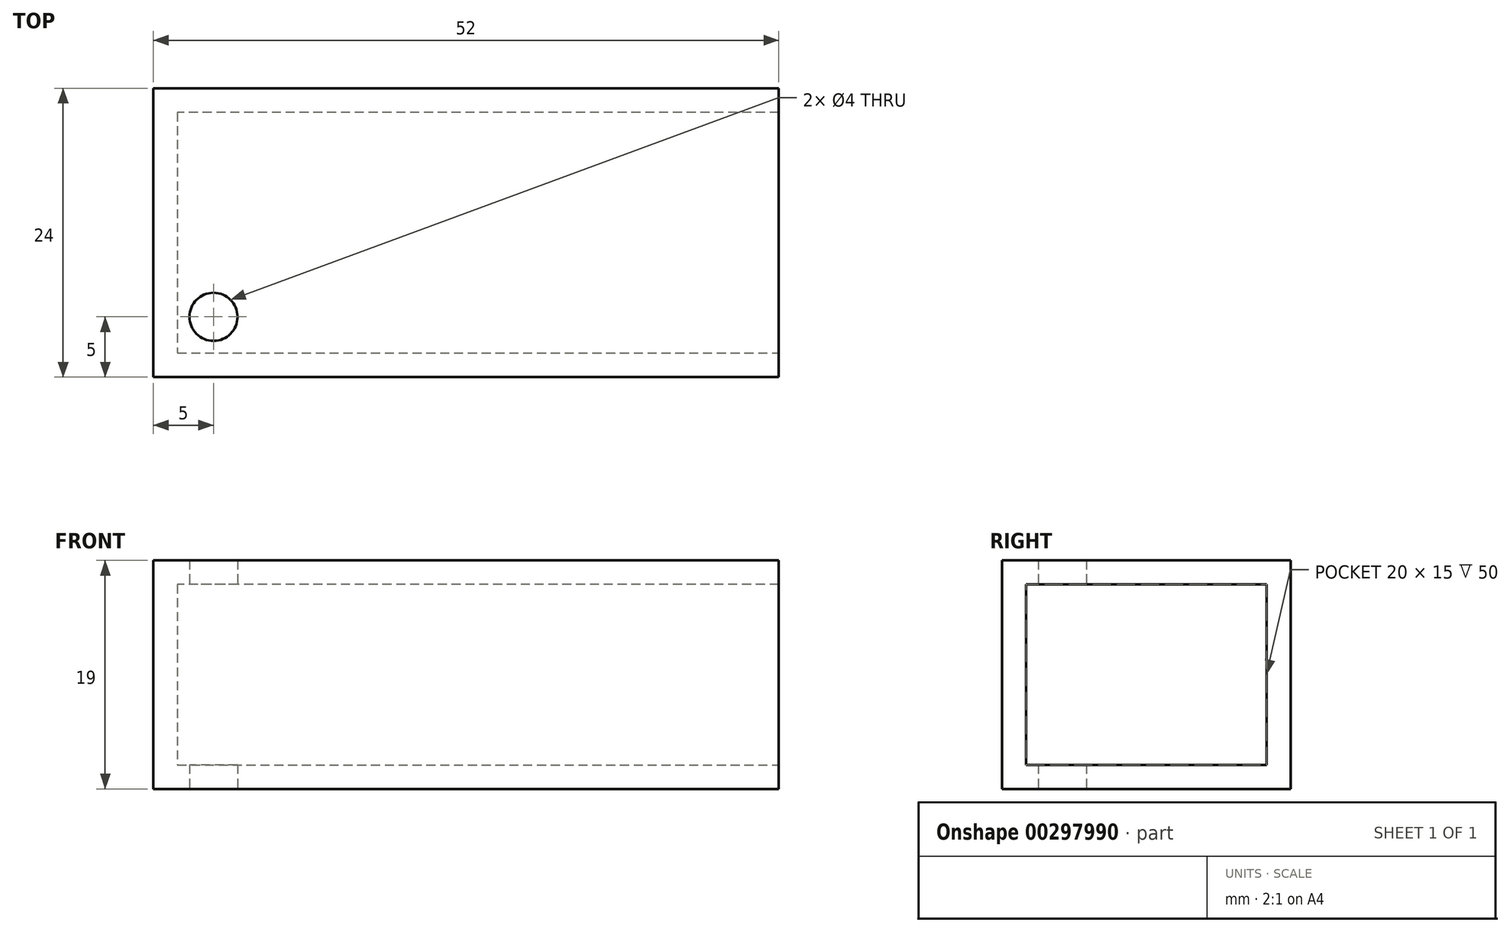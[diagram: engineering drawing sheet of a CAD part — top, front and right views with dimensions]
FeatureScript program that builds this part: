
annotation { "Feature Type Name" : "Feature", "Feature Type Description" : "" }
export const myFeature = defineFeature(function(context is Context, id is Id, definition is map)
    precondition{}
    {
        {
            var Q0;
            Q0=qCreatedBy(makeId("Top.planeOp"),FACE);
            var sketch = newSketch(context, id + "F0", { "sketchPlane" : qUnion([Q0])});
            skLineSegment(sketch, "E0.bottom", {"start": v(0, 0) * mm, "end": v(52, 0) * mm});
            skLineSegment(sketch, "E0.top", {"start": v(0, 24) * mm, "end": v(52, 24) * mm});
            skLineSegment(sketch, "E0.left", {"start": v(0, 0) * mm, "end": v(0, 24) * mm});
            skLineSegment(sketch, "E0.right", {"start": v(52, 0) * mm, "end": v(52, 24) * mm});
            skCircle(sketch, "E1", {"center": v(5, 5) * mm, "radius": 2 * mm});
            skSolve(sketch);
        }
        {
            var Q0;
            Q0=makeQuery(id+"F0.imprint","IMPRINT",FACE,{"disambiguationData":[TD([[makeQuery(id+"F0.imprint","IMPRINT",EDGE,{"derivedFrom":sQuery(id+"F0.wireOp",EDGE,"E0.bottom")}),1.0]])]});
            extrude(context, id + "F1", {"entities" : qUnion([Q0]), "depth" : 2 * mm});
        }
        {
            var Q0;
            Q0=makeQuery(id+"F1.opExtrude","CAP_FACE",FACE,{"disambiguationData":[OSD([sQuery(id+"F0.wireOp",EDGE,"E0.bottom"),sQuery(id+"F0.wireOp",EDGE,"E0.top"),sQuery(id+"F0.wireOp",EDGE,"E0.left"),sQuery(id+"F0.wireOp",EDGE,"E0.right"),sQuery(id+"F0.wireOp",EDGE,"E1")])],"isStart":false});
            var sketch = newSketch(context, id + "F2", { "sketchPlane" : qUnion([Q0])});
            skLineSegment(sketch, "E2.0.0", {"start": v(52, 24) * mm, "end": v(0, 24) * mm});
            skLineSegment(sketch, "E2.0.1", {"start": v(0, 24) * mm, "end": v(0, 0) * mm});
            skLineSegment(sketch, "E2.0.2", {"start": v(0, 0) * mm, "end": v(52, 0) * mm});
            skLineSegment(sketch, "E2.0.3", {"start": v(52, 0) * mm, "end": v(52, 24) * mm});
            skLineSegment(sketch, "E3.0", {"start": v(50, 22) * mm, "end": v(2, 22) * mm});
            skLineSegment(sketch, "E3.1", {"start": v(50, 2) * mm, "end": v(50, 22) * mm});
            skLineSegment(sketch, "E3.2", {"start": v(2, 2) * mm, "end": v(50, 2) * mm});
            skLineSegment(sketch, "E3.3", {"start": v(2, 22) * mm, "end": v(2, 2) * mm});
            skSolve(sketch);
        }
        {
            var Q0;
            Q0 = qSketchRegion(id + "F2", true);
            extrude(context, id + "F3", {"entities" : qUnion([Q0]), "operationType" : NewBodyOperationType.ADD, "depth" : 15 * mm});
        }
        {
            var Q0;
            Q0=makeQuery(id+"F3.opExtrude","CAP_FACE",FACE,{"disambiguationData":[OSD([sQuery(id+"F2.wireOp",EDGE,"E2.0.0"),sQuery(id+"F2.wireOp",EDGE,"E2.0.1"),sQuery(id+"F2.wireOp",EDGE,"E2.0.2"),sQuery(id+"F2.wireOp",EDGE,"E2.0.3"),sQuery(id+"F2.wireOp",EDGE,"E3.0"),sQuery(id+"F2.wireOp",EDGE,"E3.1"),sQuery(id+"F2.wireOp",EDGE,"E3.2"),sQuery(id+"F2.wireOp",EDGE,"E3.3")])],"isStart":false});
            var sketch = newSketch(context, id + "F4", { "sketchPlane" : qUnion([Q0])});
            skLineSegment(sketch, "E4.0.0", {"start": v(52, 24) * mm, "end": v(0, 24) * mm});
            skLineSegment(sketch, "E4.0.1", {"start": v(0, 24) * mm, "end": v(0, 0) * mm});
            skLineSegment(sketch, "E4.0.2", {"start": v(0, 0) * mm, "end": v(52, 0) * mm});
            skLineSegment(sketch, "E4.0.3", {"start": v(52, 0) * mm, "end": v(52, 24) * mm});
            skCircle(sketch, "E5.0", {"center": v(5, 5) * mm, "radius": 2 * mm});
            skSolve(sketch);
        }
        {
            var Q0;
            Q0 = qSketchRegion(id + "F4", true);
            extrude(context, id + "F5", {"entities" : qUnion([Q0]), "operationType" : NewBodyOperationType.ADD, "depth" : 2 * mm});
        }
        {
            var Q0;
            Q0=makeQuery(id+"F5.boolean.opBoolean","MERGE",FACE,{"derivedFrom":[makeQuery(id+"F3.boolean.opBoolean","MERGE",FACE,{"derivedFrom":[makeQuery(id+"F1.opExtrude","SWEPT_FACE",FACE,{"disambiguationData":[OSD([sQuery(id+"F0.wireOp",EDGE,"E0.right")])]}),makeQuery(id+"F3.opExtrude","SWEPT_FACE",FACE,{"disambiguationData":[OSD([sQuery(id+"F2.wireOp",EDGE,"E2.0.3")])]})]}),makeQuery(id+"F5.opExtrude","SWEPT_FACE",FACE,{"disambiguationData":[OSD([sQuery(id+"F4.wireOp",EDGE,"E4.0.3")])]})]});
            var sketch = newSketch(context, id + "F6", { "sketchPlane" : qUnion([Q0])});
            skLineSegment(sketch, "E6.bottom", {"start": v(2, 2) * mm, "end": v(22, 2) * mm});
            skLineSegment(sketch, "E6.top", {"start": v(2, 17) * mm, "end": v(22, 17) * mm});
            skLineSegment(sketch, "E6.left", {"start": v(2, 2) * mm, "end": v(2, 17) * mm});
            skLineSegment(sketch, "E6.right", {"start": v(22, 2) * mm, "end": v(22, 17) * mm});
            skSolve(sketch);
        }
        {
            var Q0;
            Q0 = qSketchRegion(id + "F6", true);
            extrude(context, id + "F7", {"entities" : qUnion([Q0]), "operationType" : NewBodyOperationType.REMOVE, "endBound" : BoundingType.UP_TO_NEXT, "oppositeDirection" : true, "depth" : 25 * mm});
        }
    });
